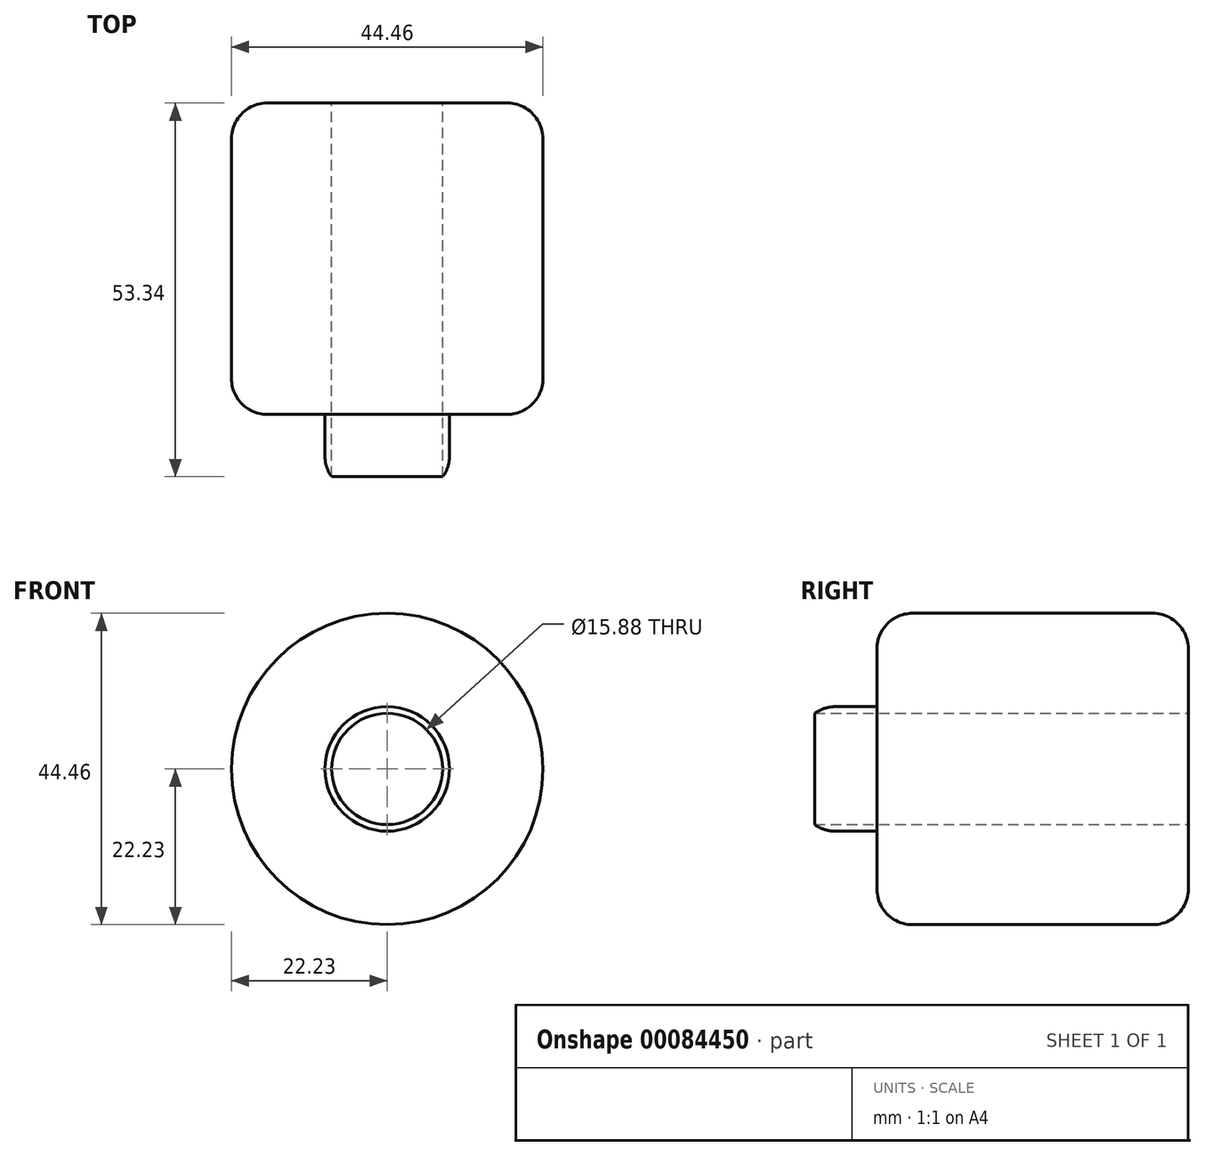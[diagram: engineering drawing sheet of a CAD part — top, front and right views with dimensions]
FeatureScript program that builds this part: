
annotation { "Feature Type Name" : "Feature", "Feature Type Description" : "" }
export const myFeature = defineFeature(function(context is Context, id is Id, definition is map)
    precondition{}
    {
        {
            var Q0;
            Q0=qCreatedBy(makeId("Front.planeOp"),FACE);
            var sketch = newSketch(context, id + "F0", { "sketchPlane" : qUnion([Q0])});
            skCircle(sketch, "E0", {"center": v(0, 0) * mm, "radius": 22.22 * mm});
            skCircle(sketch, "E1", {"center": v(0, 0) * mm, "radius": 7.94 * mm});
            skCircle(sketch, "E2", {"center": v(0, 0) * mm, "radius": 8.9 * mm});
            skSolve(sketch);
        }
        {
            var Q0;
            Q0=makeQuery(id+"F0.imprint","IMPRINT",FACE,{"disambiguationData":[TD([[makeQuery(id+"F0.imprint","IMPRINT",EDGE,{"derivedFrom":sQuery(id+"F0.wireOp",EDGE,"E1")}),-1.0]])]});
            extrude(context, id + "F1", {"entities" : qUnion([Q0]), "depth" : 53.34 * mm});
        }
        {
            var Q0;
            Q0=makeQuery(id+"F0.imprint","IMPRINT",FACE,{"disambiguationData":[TD([[makeQuery(id+"F0.imprint","IMPRINT",EDGE,{"derivedFrom":sQuery(id+"F0.wireOp",EDGE,"E0")}),1.0]])]});
            extrude(context, id + "F2", {"entities" : qUnion([Q0]), "operationType" : NewBodyOperationType.ADD, "depth" : 44.45 * mm});
        }
        {
            var Q0;
            Q0=makeQuery(id+"F2.opExtrude","CAP_EDGE",EDGE,{"disambiguationData":[OSD([sQuery(id+"F0.wireOp",EDGE,"E0")])],"isStart":false});
            fillet(context, id + "F3", {"entities" : qUnion([Q0]), "radius" : 5.08 * mm, "tangentPropagation" : true, "allowEdgeOverflow" : false});
        }
        {
            var Q0;
            Q0=makeQuery(id+"F2.opExtrude","CAP_EDGE",EDGE,{"disambiguationData":[OSD([sQuery(id+"F0.wireOp",EDGE,"E0")])],"isStart":true});
            fillet(context, id + "F4", {"entities" : qUnion([Q0]), "radius" : 5.08 * mm, "tangentPropagation" : true, "allowEdgeOverflow" : false});
        }
        {
            var Q0;
            Q0=makeQuery(id+"F1.opExtrude","CAP_EDGE",EDGE,{"disambiguationData":[OSD([sQuery(id+"F0.wireOp",EDGE,"E2")])],"isStart":false});
            fillet(context, id + "F5", {"entities" : qUnion([Q0]), "radius" : 5.08 * mm, "tangentPropagation" : true, "allowEdgeOverflow" : false});
        }
    });
